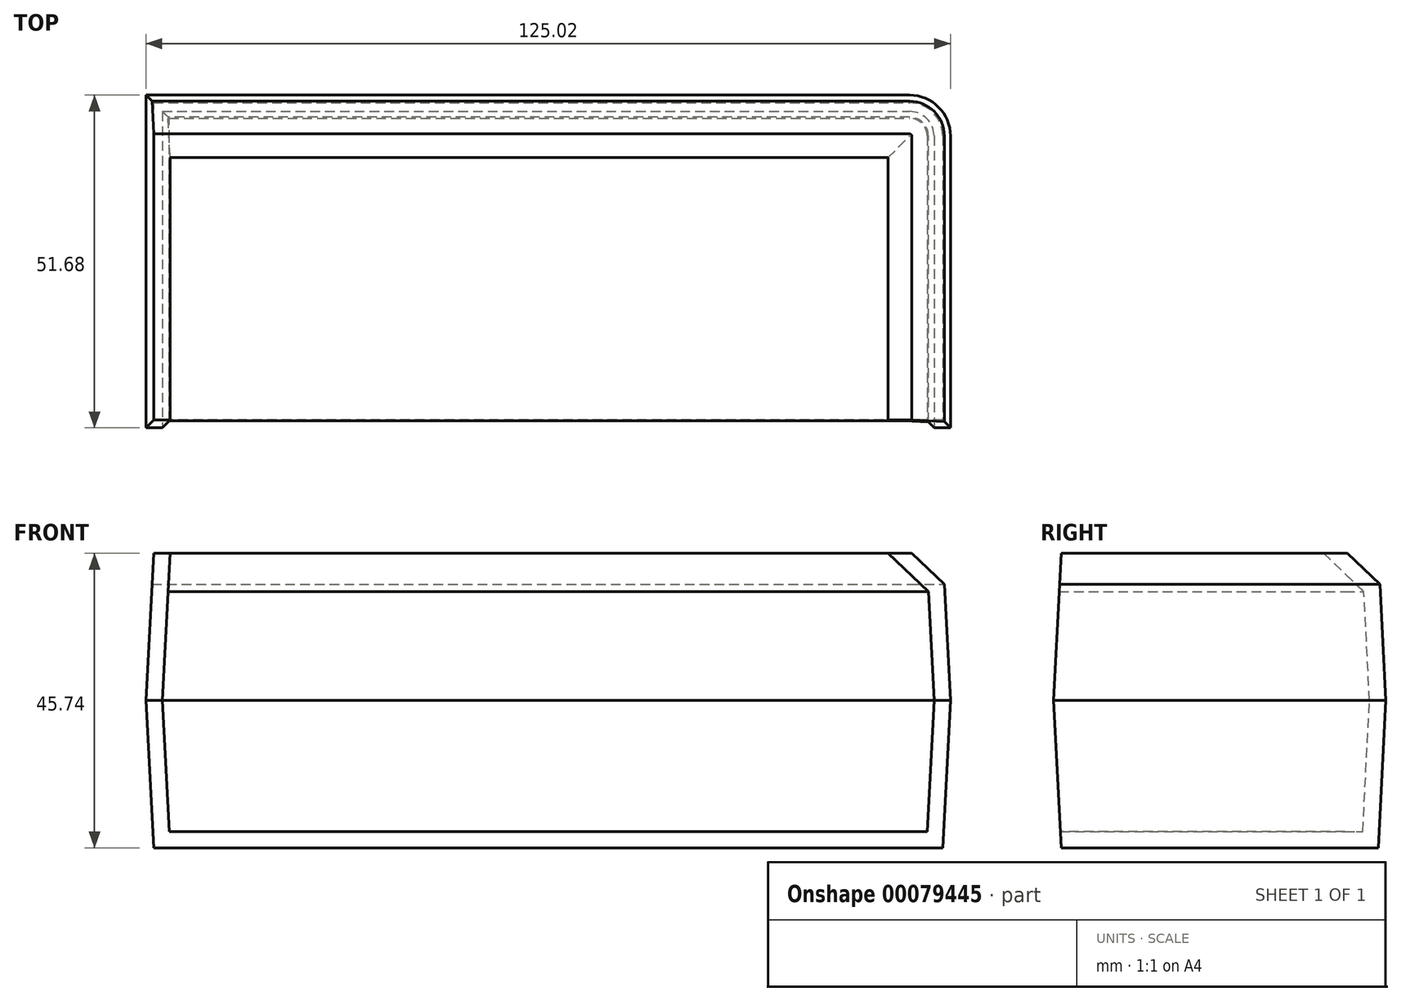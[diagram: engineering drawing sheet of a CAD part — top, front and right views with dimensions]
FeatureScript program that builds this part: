
annotation { "Feature Type Name" : "Feature", "Feature Type Description" : "" }
export const myFeature = defineFeature(function(context is Context, id is Id, definition is map)
    precondition{}
    {
        {
            var Q0;
            Q0=qCreatedBy(makeId("Top.planeOp"),FACE);
            var sketch = newSketch(context, id + "F0", { "sketchPlane" : qUnion([Q0])});
            skLineSegment(sketch, "E0.bottom", {"start": v(-125.02, 51.68) * mm, "end": v(-6.35, 51.68) * mm});
            skLineSegment(sketch, "E0.top", {"start": v(-125.02, 0) * mm, "end": v(0, 0) * mm});
            skLineSegment(sketch, "E0.left", {"start": v(-125.02, 51.68) * mm, "end": v(-125.02, 0) * mm});
            skLineSegment(sketch, "E0.right", {"start": v(0, 45.33) * mm, "end": v(0, 0) * mm});
            skPoint(sketch, "E1.visualSharp", {"position": v(0, 51.68) * mm});
            skArc(sketch, "E1.filletArc", {"start": v(0, 45.33) * mm, "mid": v(-1.86, 49.82) * mm, "end": v(-6.35, 51.68) * mm});
            skPoint(sketch, "E2.0", {"position": v(0, 0) * mm});
            skSolve(sketch);
        }
        {
            var Q0;
            Q0=makeQuery(id+"F0.imprint","IMPRINT",FACE,{"disambiguationData":[TD([[makeQuery(id+"F0.imprint","IMPRINT",EDGE,{"derivedFrom":sQuery(id+"F0.wireOp",EDGE,"E0.bottom")}),-1.0]])]});
            extrude(context, id + "F1", {"entities" : qUnion([Q0]), "endBound" : BoundingType.SYMMETRIC, "depth" : 45.75 * mm, "hasDraft" : true, "draftAngle" : 3 * degree, "draftPullDirection" : true});
        }
        {
            var Q0;
            Q0=makeQuery(id+"F1.opExtrude","CAP_EDGE",EDGE,{"disambiguationData":[OSD([sQuery(id+"F0.wireOp",EDGE,"E0.right")])],"isStart":false});
            chamfer(context, id + "F2", {"entities" : qUnion([Q0]), "width" : 5.08 * mm, "tangentPropagation" : true});
        }
        {
            var Q0;
            Q0=makeQuery(id+"F1.split0.splitOp","SPLIT",FACE,{"derivedFrom":makeQuery(id+"F1.opExtrude","SWEPT_FACE",FACE,{"disambiguationData":[OSD([sQuery(id+"F0.wireOp",EDGE,"E0.top")])]})});
            var Q1;
            Q1=makeQuery(id+"F1.opExtrude","CAP_FACE",FACE,{"disambiguationData":[OSD([sQuery(id+"F0.wireOp",EDGE,"E0.bottom"),sQuery(id+"F0.wireOp",EDGE,"E0.top"),sQuery(id+"F0.wireOp",EDGE,"E0.left"),sQuery(id+"F0.wireOp",EDGE,"E0.right"),sQuery(id+"F0.wireOp",EDGE,"E1.filletArc")])],"isStart":false});
            var Q2;
            Q2=makeQuery(id+"F1.split0.splitOp","SPLIT",FACE,{"derivedFrom":makeQuery(id+"F1.opExtrude","SWEPT_FACE",FACE,{"disambiguationData":[OSD([sQuery(id+"F0.wireOp",EDGE,"E0.top")])]}),"isFromBackBody":true});
            shell(context, id + "F3", {"entities" : qUnion([Q0, Q1, Q2]), "thickness" : 2.54 * mm});
        }
    });
